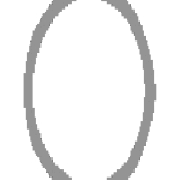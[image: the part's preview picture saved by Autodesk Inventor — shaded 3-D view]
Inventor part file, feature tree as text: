
AUTODESK INVENTOR PART (.ipt)
format: ipt  version: 2021 (Build 250183000, 183)  size: 109,568 bytes
history: native  units: in
note: dims shown in document units (in); Inventor stores cm internally (conversion verified against a paired STEP export)
features: other x4, sketch x3, plane x1
ambient origin geometry x8: Origin, YZ Plane, XZ Plane, XY Plane, X Axis, Y Axis, Z Axis, Center Point
bodies: Solid1 (feature_tree), Body (feature_tree)
feature tree (8):
  other  "Driven Length"
  other  "Frame Generator"
  other  "Start Plane"
  other  "End Plane"
  sketch  "Sketch"  dims[d2=30.4537in d4=-0.0in d5=30.4537in d6=0.12in d7=0.0in d8=90.0deg d9=30.4537in]
  sketch  "Sketch2"  dims[d0=1.0in]
  plane  "Work Plane3"
  sketch  "Sketch3"  dims[d1=0.065in]
